# Revit family: BENCH_PRIMARY_4P-5P
name_source: partatom
category: Furniture
units: mm (PartAtom-declared; Revit-internal decimal feet)

## family parameters
Always vertical = Yes
Cut with Voids When Loaded = No
OmniClass Number = 23.40.20.00
OmniClass Title = General Furniture and Specialties
Room Calculation Point = No
Shared = No
Work Plane-Based = No

## types (42) — shared parameters
ADDITIONAL = No
CUTOUT_WT = No
FULL_WT = Yes
Manufacturer = IBR InnovaSystem
URL = https://ibr-innovasystem.com
WT_12-75_XL = No
WT_15-75_XL = No
WT_6-75_XL = No
WT_9-75_XL = No
XL_WORKTOP = No
zero-valued in all types: Default Elevation

## per-type parameters (varying)
| type | Description | HEIGHT | LOW_TAG | Length | WT_12-75 | WT_15-75 | WT_6-75 | WT_9-75 | depth | midleg |
| PRB-15759 | Primary Bench 1500x750x900 | 900 mm  [stored 2.95276 ft] | No | 1500 mm  [stored 4.92126 ft] | No | Yes | No | No | 750 mm  [stored 2.46063 ft] | No |
| PRB-15909 | Primary Bench 1500x900x900 | 900 mm  [stored 2.95276 ft] | No | 1500 mm  [stored 4.92126 ft] | No | Yes | No | No | 900 mm  [stored 2.95276 ft] | No |
| PRB-15609 | Primary Bench 1500x600x900 | 900 mm  [stored 2.95276 ft] | No | 1500 mm  [stored 4.92126 ft] | No | Yes | No | No | 600 mm | No |
| PRB-15757 | Primary Bench 1500x750x750 | 750 mm  [stored 2.46063 ft] | Yes | 1500 mm  [stored 4.92126 ft] | No | Yes | No | No | 750 mm  [stored 2.46063 ft] | No |
| PRB-15907 | Primary Bench 1500x900x750 | 750 mm  [stored 2.46063 ft] | Yes | 1500 mm  [stored 4.92126 ft] | No | Yes | No | No | 900 mm  [stored 2.95276 ft] | No |
| PRB-15607 | Primary Bench 1500x600x750 | 750 mm  [stored 2.46063 ft] | Yes | 1500 mm  [stored 4.92126 ft] | No | Yes | No | No | 600 mm | No |
| PRB-12759 | Primary Bench 1200x750x900 | 900 mm  [stored 2.95276 ft] | No | 1200 mm | Yes | No | No | No | 750 mm  [stored 2.46063 ft] | No |
| PRB-12909 | Primary Bench 1200x900x900 | 900 mm  [stored 2.95276 ft] | No | 1200 mm | Yes | No | No | No | 900 mm  [stored 2.95276 ft] | No |
| PRB-12609 | Primary Bench 1200x600x900 | 900 mm  [stored 2.95276 ft] | No | 1200 mm | Yes | No | No | No | 600 mm | No |
| PRB-12757 | Primary Bench 1200x750x750 | 750 mm  [stored 2.46063 ft] | Yes | 1200 mm | Yes | No | No | No | 750 mm  [stored 2.46063 ft] | No |
| PRB-12907 | Primary Bench 1200x900x750 | 750 mm  [stored 2.46063 ft] | Yes | 1200 mm | Yes | No | No | No | 900 mm  [stored 2.95276 ft] | No |
| PRB-12607 | Primary Bench 1200x600x750 | 750 mm  [stored 2.46063 ft] | Yes | 1200 mm | Yes | No | No | No | 600 mm | No |
| PRB-09759 | Primary Bench 900x750x900 | 900 mm  [stored 2.95276 ft] | No | 900 mm  [stored 2.95276 ft] | No | No | No | Yes | 750 mm  [stored 2.46063 ft] | No |
| PRB-09909 | Primary Bench 900x900x900 | 900 mm  [stored 2.95276 ft] | No | 900 mm  [stored 2.95276 ft] | No | No | No | Yes | 900 mm  [stored 2.95276 ft] | No |
| PRB-09609 | Primary Bench 900x600x900 | 900 mm  [stored 2.95276 ft] | No | 900 mm  [stored 2.95276 ft] | No | No | No | Yes | 600 mm | No |
| PRB-09757 | Primary Bench 900x750x750 | 750 mm  [stored 2.46063 ft] | Yes | 900 mm  [stored 2.95276 ft] | No | No | No | Yes | 750 mm  [stored 2.46063 ft] | No |
| PRB-09907 | Primary Bench 900x900x750 | 750 mm  [stored 2.46063 ft] | Yes | 900 mm  [stored 2.95276 ft] | No | No | No | Yes | 900 mm  [stored 2.95276 ft] | No |
| PRB-09607 | Primary Bench 900x600x750 | 750 mm  [stored 2.46063 ft] | Yes | 900 mm  [stored 2.95276 ft] | No | No | No | Yes | 600 mm | No |
| PRB-06759 | Primary Bench 600x750x900 | 900 mm  [stored 2.95276 ft] | No | 600 mm | No | No | Yes | No | 750 mm  [stored 2.46063 ft] | No |
| PRB-06909 | Primary Bench 600x900x900 | 900 mm  [stored 2.95276 ft] | No | 600 mm | No | No | Yes | No | 900 mm  [stored 2.95276 ft] | No |
| PRB-06609 | Primary Bench 600x600x900 | 900 mm  [stored 2.95276 ft] | No | 600 mm | No | No | Yes | No | 600 mm | No |
| PRB-06757 | Primary Bench 600x750x750 | 750 mm  [stored 2.46063 ft] | Yes | 600 mm | No | No | Yes | No | 750 mm  [stored 2.46063 ft] | No |
| PRB-06907 | Primary Bench 600x900x750 | 750 mm  [stored 2.46063 ft] | Yes | 600 mm | No | No | Yes | No | 900 mm  [stored 2.95276 ft] | No |
| PRB-06607 | Primary Bench 600x600x750 | 750 mm  [stored 2.46063 ft] | Yes | 600 mm | No | No | Yes | No | 600 mm | No |
| PRB5-18759 | Primary Bench 5P 1800x750x900 | 900 mm  [stored 2.95276 ft] | No | 1800 mm  [stored 5.90551 ft] | No | No | No | No | 750 mm  [stored 2.46063 ft] | Yes |
| PRB5-18909 | Primary Bench 5P 1800x900x900 | 900 mm  [stored 2.95276 ft] | No | 1800 mm  [stored 5.90551 ft] | No | No | No | No | 900 mm  [stored 2.95276 ft] | Yes |
| PRB5-18609 | Primary Bench 5P 1800x600x900 | 900 mm  [stored 2.95276 ft] | No | 1800 mm  [stored 5.90551 ft] | No | No | No | No | 600 mm | Yes |
| PRB5-18757 | Primary Bench 5P 1800x750x750 | 750 mm  [stored 2.46063 ft] | Yes | 1800 mm  [stored 5.90551 ft] | No | No | No | No | 750 mm  [stored 2.46063 ft] | Yes |
| PRB5-18607 | Primary Bench 5P 1800x600x750 | 750 mm  [stored 2.46063 ft] | Yes | 1800 mm  [stored 5.90551 ft] | No | No | No | No | 600 mm | Yes |
| PRB5-18907 | Primary Bench 5P 1800x900x750 | 750 mm  [stored 2.46063 ft] | Yes | 1800 mm  [stored 5.90551 ft] | No | No | No | No | 900 mm  [stored 2.95276 ft] | Yes |
| PRB5-21759 | Primary Bench 5P 2100x750x900 | 900 mm  [stored 2.95276 ft] | No | 2100 mm | No | No | No | No | 750 mm  [stored 2.46063 ft] | Yes |
| PRB5-21909 | Primary Bench 5P 2100x900x900 | 900 mm  [stored 2.95276 ft] | No | 2100 mm | No | No | No | No | 900 mm  [stored 2.95276 ft] | Yes |
| PRB5-21609 | Primary Bench 5P 2100x600x900 | 900 mm  [stored 2.95276 ft] | No | 2100 mm | No | No | No | No | 600 mm | Yes |
| PRB5-21757 | Primary Bench 5P 2100x750x750 | 750 mm  [stored 2.46063 ft] | Yes | 2100 mm | No | No | No | No | 750 mm  [stored 2.46063 ft] | Yes |
| PRB5-21607 | Primary Bench 5P 2100x600x750 | 750 mm  [stored 2.46063 ft] | Yes | 2100 mm | No | No | No | No | 750 mm  [stored 2.46063 ft] | Yes |
| PRB5-21907 | Primary Bench 5P 2100x900x750 | 750 mm  [stored 2.46063 ft] | Yes | 2100 mm | No | No | No | No | 900 mm  [stored 2.95276 ft] | Yes |
| PRB5-24759 | Primary Bench 5P 2400x750x900 | 900 mm  [stored 2.95276 ft] | No | 2400 mm  [stored 7.87402 ft] | No | No | No | No | 750 mm  [stored 2.46063 ft] | Yes |
| PRB5-24909 | Primary Bench 5P 2400x900x900 | 900 mm  [stored 2.95276 ft] | No | 2400 mm  [stored 7.87402 ft] | No | No | No | No | 900 mm  [stored 2.95276 ft] | Yes |
| PRB5-24609 | Primary Bench 5P 2400x600x900 | 900 mm  [stored 2.95276 ft] | No | 2400 mm  [stored 7.87402 ft] | No | No | No | No | 600 mm | Yes |
| PRB5-24756 | Primary Bench 5P 2400x750x750 | 750 mm  [stored 2.46063 ft] | Yes | 2400 mm  [stored 7.87402 ft] | No | No | No | No | 750 mm  [stored 2.46063 ft] | Yes |
| PRB5-24907 | Primary Bench 5P 2400x900x750 | 750 mm  [stored 2.46063 ft] | Yes | 2400 mm  [stored 7.87402 ft] | No | No | No | No | 900 mm  [stored 2.95276 ft] | Yes |
| PRB5-24607 | Primary Bench 5P 2400x600x750 | 750 mm  [stored 2.46063 ft] | Yes | 2400 mm  [stored 7.87402 ft] | No | No | No | No | 600 mm | Yes |

note: [stored X ft] marks values corroborated as IEEE doubles in the binary element streams (Revit-internal decimal feet)

## geometry (parser evidence)
native form markers: Sweep x9
no freeform markers — native parametric forms only
